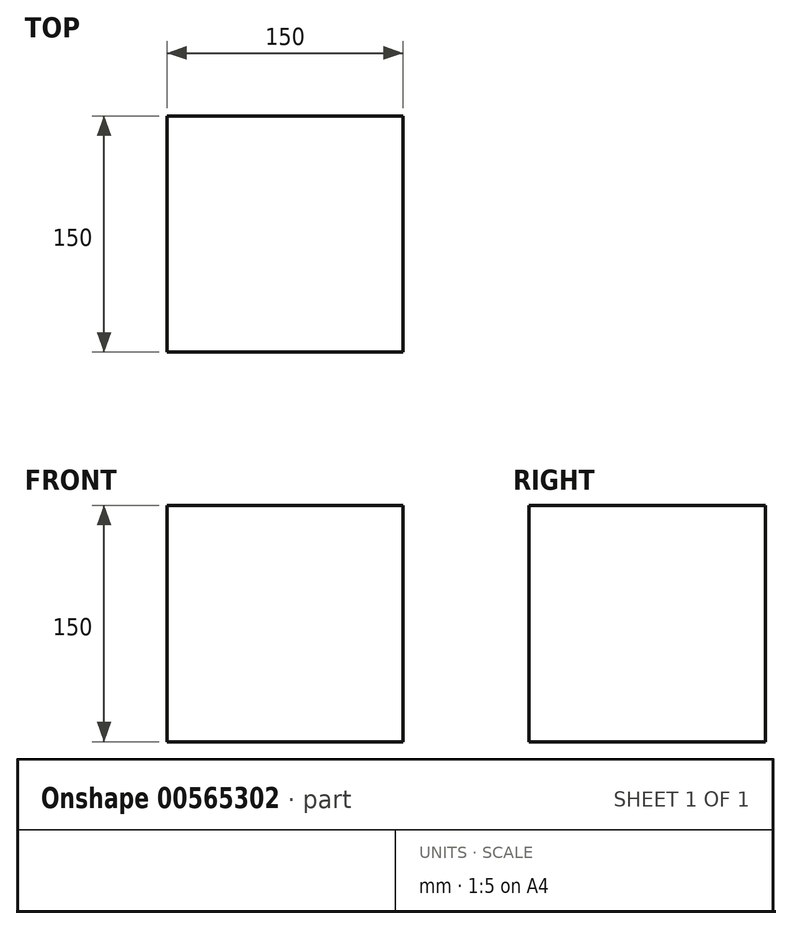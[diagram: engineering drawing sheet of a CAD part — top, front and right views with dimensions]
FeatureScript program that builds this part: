
annotation { "Feature Type Name" : "Feature", "Feature Type Description" : "" }
export const myFeature = defineFeature(function(context is Context, id is Id, definition is map)
    precondition{}
    {
        {
            var Q0;
            Q0=qCreatedBy(makeId("Top.planeOp"),FACE);
            var sketch = newSketch(context, id + "F0", { "sketchPlane" : qUnion([Q0])});
            skLineSegment(sketch, "E0.bottom", {"start": v(0, 0) * mm, "end": v(150, 0) * mm});
            skLineSegment(sketch, "E0.top", {"start": v(0, 150) * mm, "end": v(150, 150) * mm});
            skLineSegment(sketch, "E0.left", {"start": v(0, 0) * mm, "end": v(0, 150) * mm});
            skLineSegment(sketch, "E0.right", {"start": v(150, 0) * mm, "end": v(150, 150) * mm});
            skSolve(sketch);
        }
        {
            var Q0;
            Q0=makeQuery(id+"F0.imprint","IMPRINT",FACE,{"disambiguationData":[TD([[makeQuery(id+"F0.imprint","IMPRINT",EDGE,{"derivedFrom":sQuery(id+"F0.wireOp",EDGE,"E0.bottom")}),1.0]])]});
            extrude(context, id + "F1", {"entities" : qUnion([Q0]), "depth" : 150 * mm});
        }
    });
